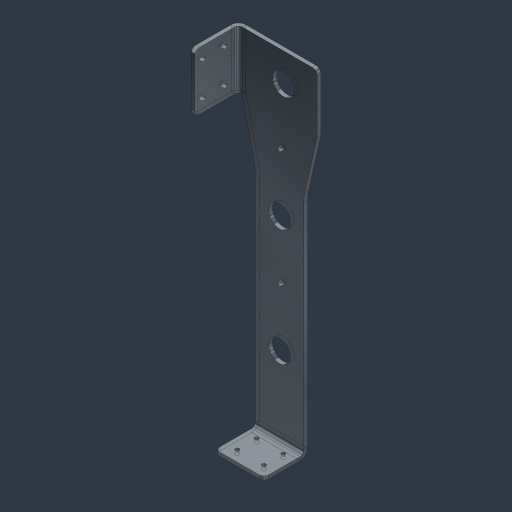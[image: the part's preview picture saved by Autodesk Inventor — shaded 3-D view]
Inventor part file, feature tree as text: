
AUTODESK INVENTOR PART (.ipt)
format: ipt  version: 2024.3 (Build 283343000, 343)  size: 190,976 bytes
history: native  units: mm (DEFAULTED — no unit token found)
features: other x4, sketch x3
ambient origin geometry x8: Origin, YZ Plane, XZ Plane, XY Plane, X Axis, Y Axis, Z Axis, Center Point
bodies: Solid1 (feature_tree)
feature tree (7):
  other  "feeder_guide_plate.ipt"
  other  "Solid1::feeder_guide_plate.ipt"
  other  "TaggingFeature1"
  sketch  "Sketch1"  dims[d0=10.0mm]
  sketch  "Sketch2"  dims[d1=4.7625mm]
  sketch  "Sketch3"
  other  "Definition1"
